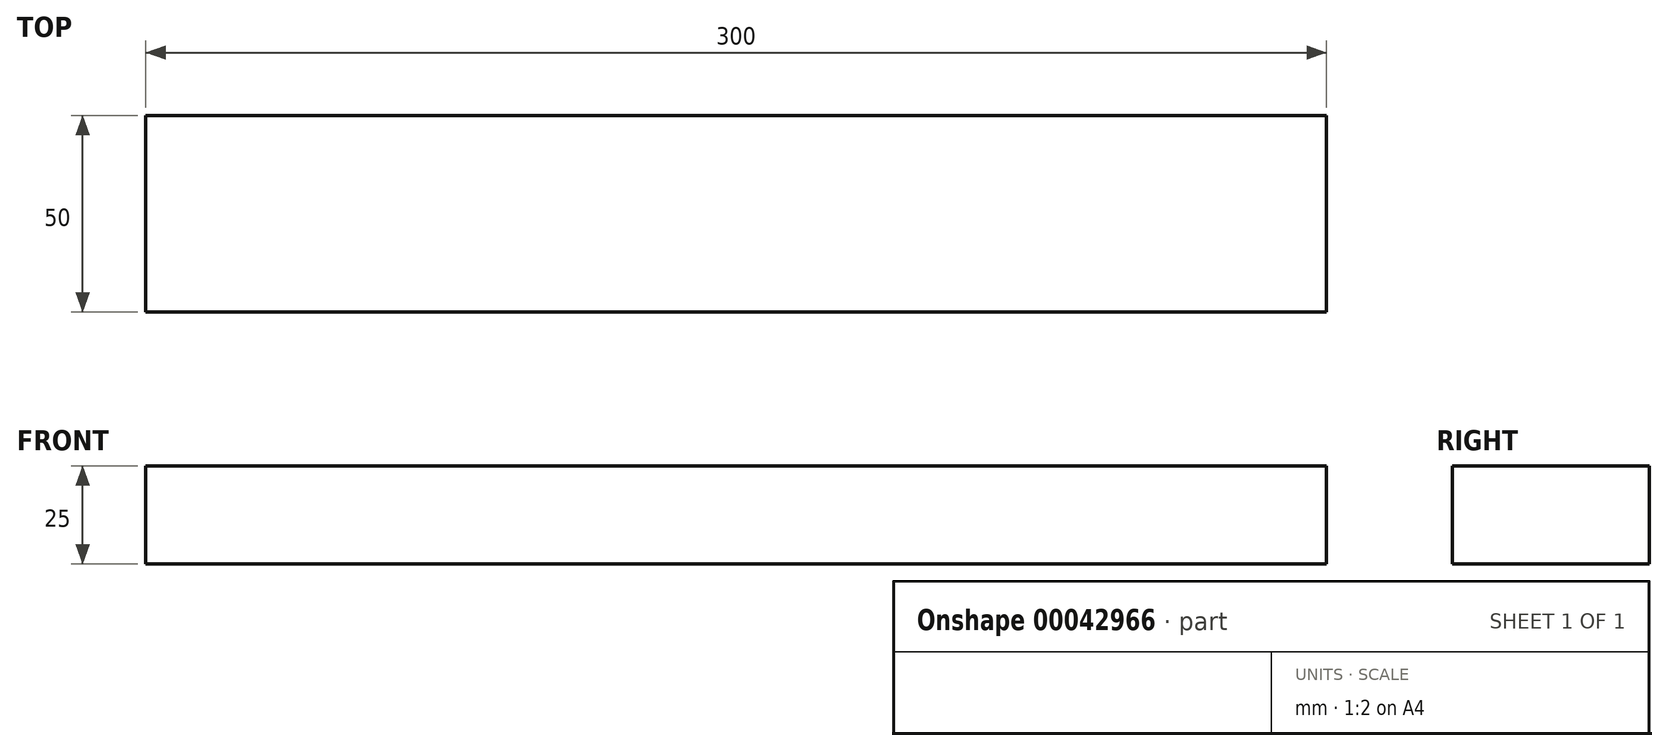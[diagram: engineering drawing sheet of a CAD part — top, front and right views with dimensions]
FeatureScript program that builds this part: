
annotation { "Feature Type Name" : "Feature", "Feature Type Description" : "" }
export const myFeature = defineFeature(function(context is Context, id is Id, definition is map)
    precondition{}
    {
        {
            var Q0;
            Q0=qCreatedBy(makeId("Top.planeOp"),FACE);
            var sketch = newSketch(context, id + "F0", { "sketchPlane" : qUnion([Q0])});
            skLineSegment(sketch, "E0.bottom", {"start": v(0, 0) * mm, "end": v(-300, 0) * mm});
            skLineSegment(sketch, "E0.top", {"start": v(0, 50) * mm, "end": v(-300, 50) * mm});
            skLineSegment(sketch, "E0.left", {"start": v(0, 0) * mm, "end": v(0, 50) * mm});
            skLineSegment(sketch, "E0.right", {"start": v(-300, 0) * mm, "end": v(-300, 50) * mm});
            skLineSegment(sketch, "E1", {"start": v(-309.82, 22.87) * mm, "end": v(20.15, 22.87) * mm, "construction": true});
            skSolve(sketch);
        }
        {
            var Q0;
            Q0 = qSketchRegion(id + "F0", true);
            extrude(context, id + "F1", {"entities" : qUnion([Q0]), "depth" : 25 * mm});
        }
    });
